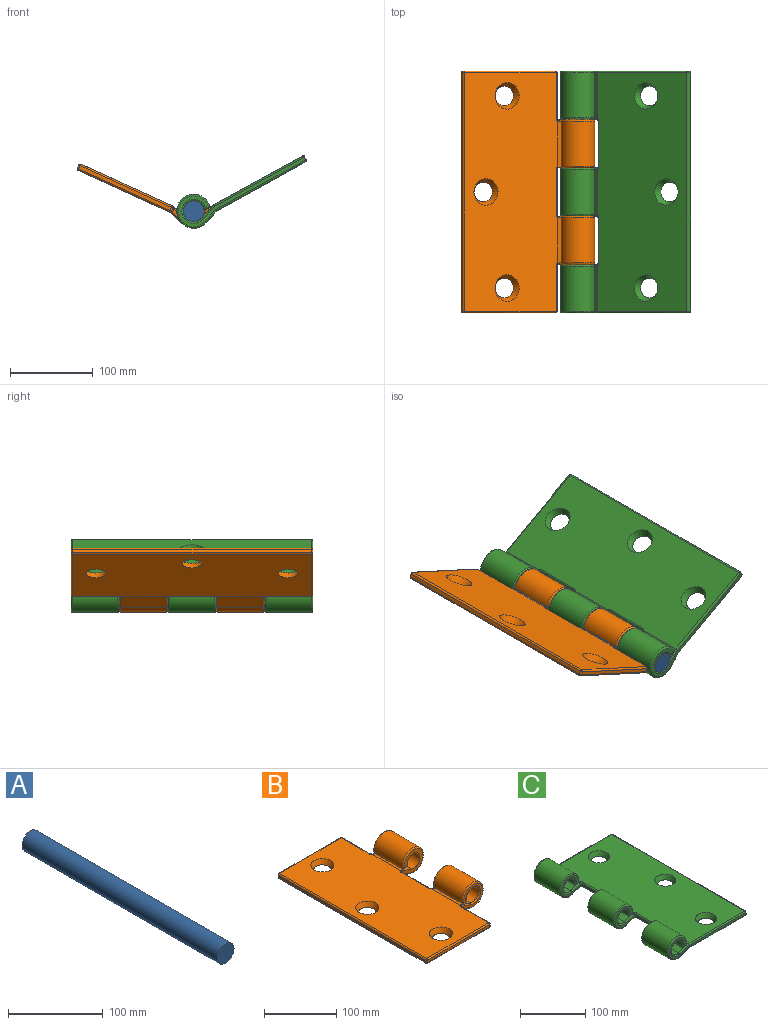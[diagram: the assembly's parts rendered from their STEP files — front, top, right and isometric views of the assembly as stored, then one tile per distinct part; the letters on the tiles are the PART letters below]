
ASSEMBLY  parts=3 mates=2
PART A: 3 faces, bbox 25x292x25 mm
  f0: cylinder r=12.5mm len=292mm, axis (0,-1,0), area 22933.6mm2, adj f1,f2
  f1: plane 25x25mm, normal (0,1,0), area 490.9mm2, adj f0
  f2: plane 25x25mm, normal (0,-1,0), area 490.9mm2, adj f0
PART B: 86 faces, bbox 171.7x292x44.4 mm
  f0: cylinder r=12.5mm len=54.4mm, axis (0,1,0), area 3703.3mm2, adj f2,f8,f65,f78
  f1: cylinder r=12.5mm len=56.4mm, axis (0,1,0), area 3837.4mm2, adj f3,f9,f21,f33,f71
  f2: plane 56.21x20.54mm, normal (0.32,0,0.95), area 1179.8mm2, adj f0,f12,f66,f67,f68,f72,f74,f76
  f3: plane 57.3x20.54mm, normal (0.32,0,0.95), area 1220.4mm2, adj f1,f12,f21,f35,f37,f39,f69
  f4: plane 54.85x17.59mm, normal (-0.34,0,-0.94), area 1016.5mm2, adj f6,f14,f55,f58,f84,f85
  f5: plane 54.85x17.59mm, normal (-0.34,0,-0.94), area 1016.5mm2, adj f7,f14,f30,f32,f75,f77
  f6: cylinder r=20.5mm len=54.4mm, axis (0,1,0), area 5913.6mm2, adj f4,f8,f61,f82
  f7: cylinder r=20.5mm len=54.4mm, axis (0,1,0), area 5913.6mm2, adj f5,f9,f29,f73
  f8: plane 54.4x8.42mm, normal (0,0,-1), area 458.3mm2, adj f0,f6,f63,f80
  f9: plane 54.4x8.42mm, normal (0,0,-1), area 458.3mm2, adj f1,f7,f31,f71
  f10: plane 121x4mm, normal (0,-1,0), area 484mm2, adj f52,f53,f59,f60
  f11: plane 121x4mm, normal (0,1,0), area 484mm2, adj f40,f41,f46,f47
  f12: plane 288x123mm, normal (0,0,1), area 32665.2mm2, adj f2,f3,f15,f16,f17,f39,f42,f47
  f13: plane 288x4mm, normal (-1,0,0), area 1152mm2, adj f45,f46,f53,f54
  f14: plane 288x123.06mm, normal (0,0,-1), area 33720.8mm2, adj f4,f5,f15,f16,f17,f32,f34,f36
  f15: cone r=12mm half-angle=26.6deg, axis (0,0,1), area 786.8mm2, adj f12,f14
  f16: cone r=16mm half-angle=26.6deg, axis (0,0,1), area 786.8mm2, adj f12,f14
  f17: cone r=12mm half-angle=26.6deg, axis (0,0,1), area 786.8mm2, adj f12,f14
  f18: plane 54.4x4mm, normal (1,0,0), area 217.6mm2, adj f25,f36,f41,f42
  f19: plane 41x37mm, normal (0,1,0), area 413.9mm2, adj f25,f29,f30,f31,f33,f35
  f20: plane 54.4x4mm, normal (1,0,0), area 217.6mm2, adj f26,f27,f70,f81
  f21: plane 41.04x37.04mm, normal (0,-1,0), area 593.6mm2, adj f1,f3,f26,f69,f71,f73,f75
  f22: plane 41x37mm, normal (0,1,0), area 413.9mm2, adj f27,f76,f78,f80,f82,f84
  f23: plane 54.4x4mm, normal (1,0,0), area 217.6mm2, adj f28,f51,f59,f64
  f24: plane 41x37mm, normal (0,-1,0), area 413.9mm2, adj f28,f58,f61,f63,f65,f67
  f25: cylinder r=2mm len=4.59mm, axis (0,0,1), area 12.3mm2, adj f18,f19,f32,f34,f37,f39
  f26: cylinder r=2mm len=4.59mm, axis (0,0,-1), area 12.8mm2, adj f20,f21,f69,f77,f79
  f27: cylinder r=2mm len=4.59mm, axis (0,0,1), area 12.3mm2, adj f20,f22,f72,f74,f83,f85
  f28: cylinder r=2mm len=4.59mm, axis (0,0,-1), area 12.3mm2, adj f23,f24,f50,f55,f66,f68
  f29: torus R=18.5mm, axis (0,-1,0), area 326.9mm2, adj f7,f19,f30,f31
  f30: cylinder r=2mm len=16.94mm, axis (0.94,0,-0.34), area 54.3mm2, adj f5,f19,f29,f32
  f31: cylinder r=2mm len=8.42mm, axis (1,0,0), area 19.6mm2, adj f9,f19,f29,f33
  f32: bspline ~2.47x2.33mm, area 3.5mm2, adj f5,f14,f25,f30,f34
  f33: torus R=14.5mm, axis (0,-1,0), area 222mm2, adj f1,f19,f31,f35
  f34: torus R=4mm, axis (0,0,1), area 9.2mm2, adj f14,f25,f32,f36
  f35: cylinder r=2mm len=18.54mm, axis (-0.95,0,0.32), area 59.3mm2, adj f3,f19,f33,f37
  f36: cylinder r=2mm len=54.4mm, axis (0,-1,0), area 170.9mm2, adj f14,f18,f34,f38
  f37: bspline ~3.65x3.11mm, area 6mm2, adj f3,f25,f35,f39
  f38: sphere r=2mm, area 6.3mm2, adj f36,f40,f41
  f39: torus R=4mm, axis (0,0,-1), area 8.7mm2, adj f3,f12,f25,f37,f42
  f40: cylinder r=2mm len=121mm, axis (1,0,0), area 380.1mm2, adj f11,f14,f38,f43
  f41: cylinder r=2mm len=4mm, axis (0,0,-1), area 12.6mm2, adj f11,f18,f38,f44
  f42: cylinder r=2mm len=54.4mm, axis (0,1,0), area 170.9mm2, adj f12,f18,f39,f44
  f43: sphere r=2mm, area 6.3mm2, adj f40,f45,f46
  f44: sphere r=2mm, area 6.3mm2, adj f41,f42,f47
  f45: cylinder r=2mm len=288mm, axis (0,1,0), area 904.8mm2, adj f13,f14,f43,f48
  f46: cylinder r=2mm len=4mm, axis (0,0,-1), area 12.6mm2, adj f11,f13,f43,f49
  f47: cylinder r=2mm len=121mm, axis (-1,0,0), area 380.1mm2, adj f11,f12,f44,f49
  f48: sphere r=2mm, area 6.3mm2, adj f45,f52,f53
  f49: sphere r=2mm, area 8.6mm2, adj f46,f47,f54
  f50: torus R=4mm, axis (0,0,1), area 9.2mm2, adj f14,f28,f51,f55
  f51: cylinder r=2mm len=54.4mm, axis (0,-1,0), area 170.9mm2, adj f14,f23,f50,f56
  f52: cylinder r=2mm len=121mm, axis (-1,0,0), area 380.1mm2, adj f10,f14,f48,f56
  f53: cylinder r=2mm len=4mm, axis (0,0,1), area 12.6mm2, adj f10,f13,f48,f57
  f54: cylinder r=2mm len=288mm, axis (0,1,0), area 904.8mm2, adj f12,f13,f49,f57
  f55: bspline ~2.47x2.33mm, area 3.5mm2, adj f4,f14,f28,f50,f58
  f56: sphere r=2mm, area 6.3mm2, adj f51,f52,f59
  f57: sphere r=2mm, area 6.3mm2, adj f53,f54,f60
  f58: cylinder r=2mm len=16.94mm, axis (-0.94,0,0.34), area 54.3mm2, adj f4,f24,f55,f61
  f59: cylinder r=2mm len=4mm, axis (0,0,1), area 12.6mm2, adj f10,f23,f56,f62
  f60: cylinder r=2mm len=121mm, axis (1,0,0), area 380.1mm2, adj f10,f12,f57,f62
  f61: torus R=18.5mm, axis (0,-1,0), area 326.9mm2, adj f6,f24,f58,f63
  f62: sphere r=2mm, area 6.3mm2, adj f59,f60,f64
  f63: cylinder r=2mm len=8.42mm, axis (-1,0,0), area 19.6mm2, adj f8,f24,f61,f65
  f64: cylinder r=2mm len=54.4mm, axis (0,-1,0), area 170.9mm2, adj f12,f23,f62,f66
  f65: torus R=14.5mm, axis (0,-1,0), area 222mm2, adj f0,f24,f63,f67
  f66: torus R=4mm, axis (0,0,-1), area 8.7mm2, adj f2,f12,f28,f64,f68
  f67: cylinder r=2mm len=18.54mm, axis (0.95,0,-0.32), area 59.3mm2, adj f2,f24,f65,f68
  f68: bspline ~3.65x3.11mm, area 6mm2, adj f2,f28,f66,f67
  f69: torus R=4mm, axis (0,0,-1), area 11.9mm2, adj f3,f12,f21,f26,f70
  f70: cylinder r=2mm len=54.4mm, axis (0,1,0), area 170.9mm2, adj f12,f20,f69,f72
  f71: cylinder r=2mm len=8.42mm, axis (-1,0,0), area 22.8mm2, adj f1,f9,f21,f73
  f72: torus R=4mm, axis (0,0,-1), area 8.7mm2, adj f2,f12,f27,f70,f74
  f73: torus R=18.5mm, axis (0,-1,0), area 326.9mm2, adj f7,f21,f71,f75
  f74: bspline ~2.75x2.54mm, area 6mm2, adj f2,f27,f72,f76
  f75: cylinder r=2mm len=16.94mm, axis (-0.94,0,0.34), area 54.3mm2, adj f5,f21,f73,f77
  f76: cylinder r=2mm len=18.54mm, axis (-0.95,0,0.32), area 59.3mm2, adj f2,f22,f74,f78
  f77: bspline ~2.47x2.33mm, area 3.5mm2, adj f5,f14,f26,f75,f79
  f78: torus R=14.5mm, axis (0,-1,0), area 222mm2, adj f0,f22,f76,f80
  f79: torus R=4mm, axis (0,0,1), area 9.2mm2, adj f14,f26,f77,f81
  f80: cylinder r=2mm len=8.42mm, axis (1,0,0), area 19.6mm2, adj f8,f22,f78,f82
  f81: cylinder r=2mm len=54.4mm, axis (0,-1,0), area 170.9mm2, adj f14,f20,f79,f83
  f82: torus R=18.5mm, axis (0,-1,0), area 326.9mm2, adj f6,f22,f80,f84
  f83: torus R=4mm, axis (0,0,1), area 9.2mm2, adj f14,f27,f81,f85
  f84: cylinder r=2mm len=16.94mm, axis (0.94,0,-0.34), area 54.3mm2, adj f4,f22,f82,f85
  f85: bspline ~2.47x2.33mm, area 3.5mm2, adj f4,f14,f27,f83,f84
PART C: 95 faces, bbox 171.7x292x44.4 mm
  f0: plane 54.63x17.59mm, normal (0.34,0,-0.94), area 1016.4mm2, adj f2,f12,f42,f44,f80
  f1: plane 54.85x17.59mm, normal (0.34,0,-0.94), area 1016.5mm2, adj f3,f12,f51,f52,f62,f64
  f2: cylinder r=20.5mm len=54.4mm, axis (0,1,0), area 5913.6mm2, adj f0,f4,f40,f81
  f3: cylinder r=20.5mm len=54.4mm, axis (0,1,0), area 5913.6mm2, adj f1,f5,f49,f60
  f4: plane 54.4x8.42mm, normal (0,0,-1), area 458.3mm2, adj f2,f6,f38,f86
  f5: plane 54.4x8.42mm, normal (0,0,-1), area 458.3mm2, adj f3,f7,f47,f58
  f6: cylinder r=12.5mm len=54.4mm, axis (0,1,0), area 3703.3mm2, adj f4,f8,f36,f89
  f7: cylinder r=12.5mm len=54.4mm, axis (0,1,0), area 3703.3mm2, adj f5,f9,f45,f56
  f8: plane 55.3x20.54mm, normal (-0.32,0,0.95), area 1179mm2, adj f6,f10,f33,f34,f35,f92
  f9: plane 56.21x20.54mm, normal (-0.32,0,0.95), area 1179.8mm2, adj f7,f10,f39,f41,f43,f53,f54,f55
  f10: plane 288x123mm, normal (0,0,1), area 32774mm2, adj f8,f9,f17,f20,f21,f22,f35,f37
  f11: plane 288x4mm, normal (1,0,0), area 1152mm2, adj f83,f84,f90,f91
  f12: plane 288x123.06mm, normal (0,0,-1), area 33829.6mm2, adj f0,f1,f13,f20,f21,f22,f44,f46
  f13: plane 54.63x17.59mm, normal (0.34,0,-0.94), area 1016.4mm2, adj f12,f14,f71,f72,f75
  f14: cylinder r=20.5mm len=54.4mm, axis (0,1,0), area 5913.6mm2, adj f13,f15,f69,f73
  f15: plane 54.4x8.42mm, normal (0,0,-1), area 458.3mm2, adj f14,f16,f67,f74
  f16: cylinder r=12.5mm len=54.4mm, axis (0,1,0), area 3703.3mm2, adj f15,f17,f65,f76
  f17: plane 55.3x20.54mm, normal (-0.32,0,0.95), area 1179mm2, adj f10,f16,f59,f61,f63,f78
  f18: plane 166x37mm, normal (0,-1,0), area 913.5mm2, adj f80,f81,f85,f86,f89,f91,f92,f94
  f19: plane 166x37mm, normal (0,1,0), area 913.5mm2, adj f73,f74,f75,f76,f77,f78,f82,f83
  f20: cone r=16mm half-angle=26.6deg, axis (0,0,1), area 786.8mm2, adj f10,f12
  f21: cone r=16mm half-angle=26.6deg, axis (0,0,1), area 786.8mm2, adj f10,f12
  f22: cone r=16mm half-angle=26.6deg, axis (0,0,1), area 786.8mm2, adj f10,f12
  f23: plane 41x37mm, normal (0,1,0), area 413.9mm2, adj f29,f54,f56,f58,f60,f62
  f24: plane 54.4x4mm, normal (-1,0,0), area 217.6mm2, adj f29,f30,f57,f68
  f25: plane 41x37mm, normal (0,-1,0), area 413.9mm2, adj f30,f63,f65,f67,f69,f71
  f26: plane 41x37mm, normal (0,1,0), area 413.9mm2, adj f31,f34,f36,f38,f40,f42
  f27: plane 54.4x4mm, normal (-1,0,0), area 217.6mm2, adj f31,f32,f37,f48
  f28: plane 41x37mm, normal (0,-1,0), area 413.9mm2, adj f32,f43,f45,f47,f49,f51
  f29: cylinder r=2mm len=4.59mm, axis (0,0,1), area 12.3mm2, adj f23,f24,f53,f55,f64,f66
  f30: cylinder r=2mm len=4.59mm, axis (0,0,-1), area 12.3mm2, adj f24,f25,f59,f61,f70,f72
  f31: cylinder r=2mm len=4.59mm, axis (0,0,1), area 12.3mm2, adj f26,f27,f33,f35,f44,f46
  f32: cylinder r=2mm len=4.59mm, axis (0,0,-1), area 12.3mm2, adj f27,f28,f39,f41,f50,f52
  f33: bspline ~2.75x2.54mm, area 6mm2, adj f8,f31,f34,f35
  f34: cylinder r=2mm len=18.54mm, axis (-0.95,0,-0.32), area 59.3mm2, adj f8,f26,f33,f36
  f35: torus R=4mm, axis (0,0,-1), area 8.7mm2, adj f8,f10,f31,f33,f37
  f36: torus R=14.5mm, axis (0,1,0), area 222mm2, adj f6,f26,f34,f38
  f37: cylinder r=2mm len=54.4mm, axis (0,1,0), area 170.9mm2, adj f10,f27,f35,f39
  f38: cylinder r=2mm len=8.42mm, axis (1,0,0), area 19.6mm2, adj f4,f26,f36,f40
  f39: torus R=4mm, axis (0,0,-1), area 8.7mm2, adj f9,f10,f32,f37,f41
  f40: torus R=18.5mm, axis (0,1,0), area 326.9mm2, adj f2,f26,f38,f42
  f41: bspline ~3.65x3.11mm, area 6mm2, adj f9,f32,f39,f43
  f42: cylinder r=2mm len=16.94mm, axis (0.94,0,0.34), area 54.3mm2, adj f0,f26,f40,f44
  f43: cylinder r=2mm len=18.54mm, axis (0.95,0,0.32), area 59.3mm2, adj f9,f28,f41,f45
  f44: bspline ~2.47x2.33mm, area 3.5mm2, adj f0,f12,f31,f42,f46
  f45: torus R=14.5mm, axis (0,1,0), area 222mm2, adj f7,f28,f43,f47
  f46: torus R=4mm, axis (0,0,-1), area 9.2mm2, adj f12,f31,f44,f48
  f47: cylinder r=2mm len=8.42mm, axis (-1,0,0), area 19.6mm2, adj f5,f28,f45,f49
  f48: cylinder r=2mm len=54.4mm, axis (0,-1,0), area 170.9mm2, adj f12,f27,f46,f50
  f49: torus R=18.5mm, axis (0,1,0), area 326.9mm2, adj f3,f28,f47,f51
  f50: torus R=4mm, axis (0,0,-1), area 9.2mm2, adj f12,f32,f48,f52
  f51: cylinder r=2mm len=16.94mm, axis (-0.94,0,-0.34), area 54.3mm2, adj f1,f28,f49,f52
  f52: bspline ~2.47x2.33mm, area 3.5mm2, adj f1,f12,f32,f50,f51
  f53: bspline ~2.75x2.54mm, area 6mm2, adj f9,f29,f54,f55
  f54: cylinder r=2mm len=18.54mm, axis (-0.95,0,-0.32), area 59.3mm2, adj f9,f23,f53,f56
  f55: torus R=4mm, axis (0,0,-1), area 8.7mm2, adj f9,f10,f29,f53,f57
  f56: torus R=14.5mm, axis (0,1,0), area 222mm2, adj f7,f23,f54,f58
  f57: cylinder r=2mm len=54.4mm, axis (0,1,0), area 170.9mm2, adj f10,f24,f55,f59
  f58: cylinder r=2mm len=8.42mm, axis (1,0,0), area 19.6mm2, adj f5,f23,f56,f60
  f59: torus R=4mm, axis (0,0,-1), area 8.7mm2, adj f10,f17,f30,f57,f61
  f60: torus R=18.5mm, axis (0,1,0), area 326.9mm2, adj f3,f23,f58,f62
  f61: bspline ~3.65x3.11mm, area 6mm2, adj f17,f30,f59,f63
  f62: cylinder r=2mm len=16.94mm, axis (0.94,0,0.34), area 54.3mm2, adj f1,f23,f60,f64
  f63: cylinder r=2mm len=18.54mm, axis (0.95,0,0.32), area 59.3mm2, adj f17,f25,f61,f65
  f64: bspline ~2.47x2.33mm, area 3.5mm2, adj f1,f12,f29,f62,f66
  f65: torus R=14.5mm, axis (0,1,0), area 222mm2, adj f16,f25,f63,f67
  f66: torus R=4mm, axis (0,0,-1), area 9.2mm2, adj f12,f29,f64,f68
  f67: cylinder r=2mm len=8.42mm, axis (-1,0,0), area 19.6mm2, adj f15,f25,f65,f69
  f68: cylinder r=2mm len=54.4mm, axis (0,-1,0), area 170.9mm2, adj f12,f24,f66,f70
  f69: torus R=18.5mm, axis (0,1,0), area 326.9mm2, adj f14,f25,f67,f71
  f70: torus R=4mm, axis (0,0,-1), area 9.2mm2, adj f12,f30,f68,f72
  f71: cylinder r=2mm len=16.94mm, axis (-0.94,0,-0.34), area 54.3mm2, adj f13,f25,f69,f72
  f72: bspline ~2.47x2.33mm, area 3.5mm2, adj f12,f13,f30,f70,f71
  f73: torus R=18.5mm, axis (0,-1,0), area 326.9mm2, adj f14,f19,f74,f75
  f74: cylinder r=2mm len=8.42mm, axis (-1,0,0), area 19.6mm2, adj f15,f19,f73,f76
  f75: cylinder r=2mm len=18.59mm, axis (-0.94,0,-0.34), area 59.2mm2, adj f13,f19,f73,f77
  f76: torus R=14.5mm, axis (0,-1,0), area 222mm2, adj f16,f19,f74,f78
  f77: cylinder r=2mm len=123.35mm, axis (-1,0,0), area 387mm2, adj f12,f19,f75,f79
  f78: cylinder r=2mm len=21.18mm, axis (0.95,0,0.32), area 67.5mm2, adj f17,f19,f76,f82
  f79: sphere r=2mm, area 4mm2, adj f77,f83,f84
  f80: cylinder r=2mm len=18.59mm, axis (0.94,0,0.34), area 59.2mm2, adj f0,f18,f81,f85
  f81: torus R=18.5mm, axis (0,-1,0), area 326.9mm2, adj f2,f18,f80,f86
  f82: cylinder r=2mm len=123mm, axis (1,0,0), area 385.9mm2, adj f10,f19,f78,f87
  f83: cylinder r=2mm len=4mm, axis (0,0,-1), area 12.6mm2, adj f11,f19,f79,f87
  f84: cylinder r=2mm len=288mm, axis (0,-1,0), area 904.8mm2, adj f11,f12,f79,f88
  f85: cylinder r=2mm len=123.35mm, axis (1,0,0), area 387mm2, adj f12,f18,f80,f88
  f86: cylinder r=2mm len=8.42mm, axis (1,0,0), area 19.6mm2, adj f4,f18,f81,f89
  f87: sphere r=2mm, area 6.3mm2, adj f82,f83,f90
  f88: sphere r=2mm, area 6.3mm2, adj f84,f85,f91
  f89: torus R=14.5mm, axis (0,-1,0), area 222mm2, adj f6,f18,f86,f92
  f90: cylinder r=2mm len=288mm, axis (0,1,0), area 904.8mm2, adj f10,f11,f87,f93
  f91: cylinder r=2mm len=4mm, axis (0,0,1), area 12.6mm2, adj f11,f18,f88,f93
  f92: cylinder r=2mm len=21.18mm, axis (-0.95,0,-0.32), area 67.5mm2, adj f8,f18,f89,f94
  f93: sphere r=2mm, area 6.3mm2, adj f90,f91,f94
  f94: cylinder r=2mm len=123mm, axis (-1,0,0), area 385.9mm2, adj f10,f18,f92,f93
PLACE A at identity fixed
PLACE B rot(axis=(0,1,0),24.6deg) t=(0.14,0,10.65)mm
PLACE C rot(axis=(0,-1,0),28.8deg) t=(5.45,0,-11.2)mm
MATE revolute C.f2 <-> A.f0  axis (0,-1,0) through (24.5,-292,5)mm
MATE revolute B.f0 <-> A.f0  axis (0,-1,0) through (24.5,-233.6,5)mm
